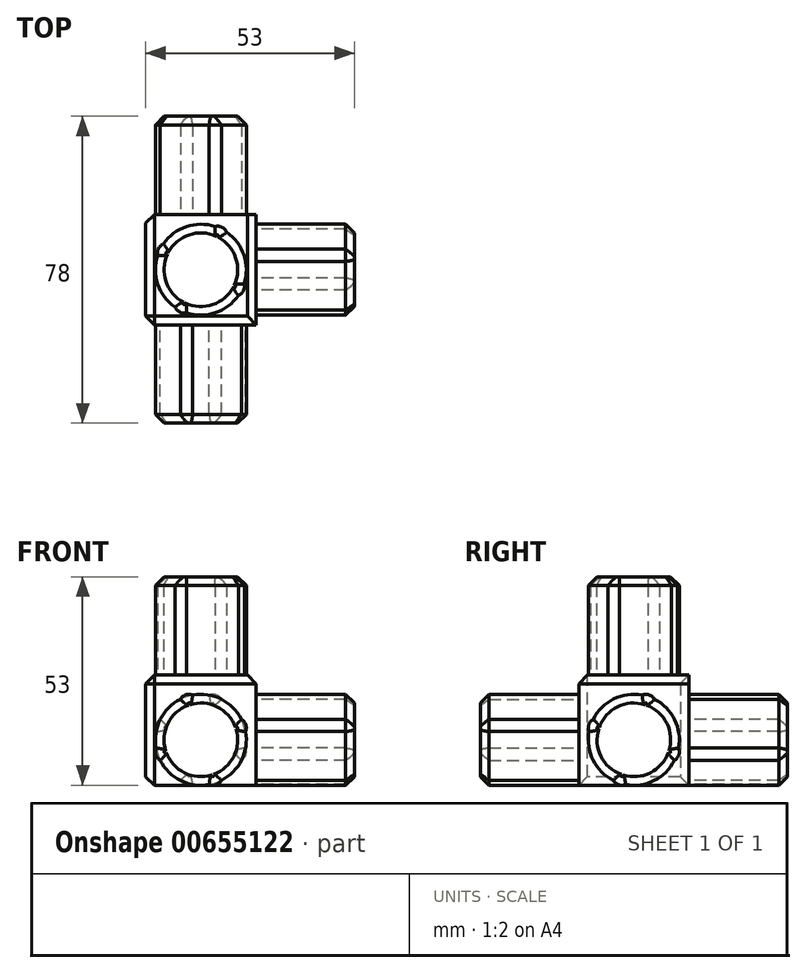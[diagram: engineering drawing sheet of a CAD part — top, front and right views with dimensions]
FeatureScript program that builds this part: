
annotation { "Feature Type Name" : "Feature", "Feature Type Description" : "" }
export const myFeature = defineFeature(function(context is Context, id is Id, definition is map)
    precondition{}
    {
        {
            var Q0;
            Q0=qCreatedBy(makeId("Front.planeOp"),FACE);
            var sketch = newSketch(context, id + "F0", { "sketchPlane" : qUnion([Q0])});
            skLineSegment(sketch, "E0.bottom", {"start": v(-14, 0) * mm, "end": v(14, 0) * mm});
            skLineSegment(sketch, "E0.top", {"start": v(-14, 28) * mm, "end": v(14, 28) * mm});
            skLineSegment(sketch, "E0.left", {"start": v(-14, 0) * mm, "end": v(-14, 28) * mm});
            skLineSegment(sketch, "E0.right", {"start": v(14, 0) * mm, "end": v(14, 28) * mm});
            skSolve(sketch);
        }
        {
            var Q0;
            Q0=qSketchRegion(id+"F0",true);
            extrude(context, id + "F1", {"entities" : qUnion([Q0]), "depth" : 28 * mm, "offsetDistance" : 25 * mm, "symmetric" : true});
        }
        {
            var Q0;
            Q0=makeQuery(id+"F1.opExtrude","CAP_FACE",FACE,{"disambiguationData":[OSD([sQuery(id+"F0.wireOp",EDGE,"E0.bottom"),sQuery(id+"F0.wireOp",EDGE,"E0.top"),sQuery(id+"F0.wireOp",EDGE,"E0.left"),sQuery(id+"F0.wireOp",EDGE,"E0.right")])],"isStart":false});
            var sketch = newSketch(context, id + "F2", { "sketchPlane" : qUnion([Q0])});
            skArc(sketch, "E1", {"start": v(-10.3, 6.34) * mm, "mid": v(-5.13, 1.2) * mm, "end": v(2.1, 0.2) * mm});
            skArc(sketch, "E2", {"start": v(-11.36, 9.46) * mm, "mid": v(-11.42, 7.7) * mm, "end": v(-10.3, 6.34) * mm});
            skArc(sketch, "E3.1.0", {"start": v(2.1, 0.2) * mm, "mid": v(3.85, 0.13) * mm, "end": v(5.2, 1.24) * mm});
            skArc(sketch, "E3.2.0", {"start": v(11.36, 13.64) * mm, "mid": v(11.42, 15.4) * mm, "end": v(10.3, 16.76) * mm});
            skArc(sketch, "E4.1.3.0", {"start": v(-2.1, 22.9) * mm, "mid": v(-3.85, 22.97) * mm, "end": v(-5.2, 21.86) * mm});
            skArc(sketch, "E5.trimOffspring", {"start": v(-5.2, 21.86) * mm, "mid": v(-10.35, 16.68) * mm, "end": v(-11.36, 9.46) * mm});
            skArc(sketch, "E6.trimOffspring", {"start": v(10.3, 16.76) * mm, "mid": v(5.13, 21.9) * mm, "end": v(-2.1, 22.9) * mm});
            skArc(sketch, "E7.trimOffspring", {"start": v(5.2, 1.24) * mm, "mid": v(10.35, 6.42) * mm, "end": v(11.36, 13.64) * mm});
            skSolve(sketch);
        }
        {
            var Q0;
            Q0=makeQuery(id+"F2.imprint","IMPRINT",FACE,{"disambiguationData":[TD([[makeQuery(id+"F2.imprint","IMPRINT",EDGE,{"derivedFrom":sQuery(id+"F2.wireOp",EDGE,"E1")}),1.0]])]});
            extrude(context, id + "F3", {"entities" : qUnion([Q0]), "operationType" : NewBodyOperationType.ADD, "depth" : 25 * mm, "offsetDistance" : 25 * mm});
        }
        {
            var Q0;
            Q0=makeQuery(id+"F1.opExtrude","SWEPT_FACE",FACE,{"disambiguationData":[OSD([sQuery(id+"F0.wireOp",EDGE,"E0.right")])]});
            var sketch = newSketch(context, id + "F4", { "sketchPlane" : qUnion([Q0])});
            skArc(sketch, "E8", {"start": v(-11.36, 13.64) * mm, "mid": v(-10.35, 6.42) * mm, "end": v(-5.2, 1.24) * mm});
            skArc(sketch, "E9", {"start": v(-10.3, 16.76) * mm, "mid": v(-11.42, 15.4) * mm, "end": v(-11.36, 13.64) * mm});
            skArc(sketch, "E10.1.0", {"start": v(-5.2, 1.24) * mm, "mid": v(-3.85, 0.13) * mm, "end": v(-2.1, 0.2) * mm});
            skArc(sketch, "E10.2.0", {"start": v(10.3, 6.34) * mm, "mid": v(11.42, 7.7) * mm, "end": v(11.36, 9.46) * mm});
            skArc(sketch, "E10.3.0", {"start": v(5.2, 21.86) * mm, "mid": v(3.85, 22.97) * mm, "end": v(2.1, 22.9) * mm});
            skArc(sketch, "E11.trimOffspring", {"start": v(2.1, 22.9) * mm, "mid": v(-5.13, 21.9) * mm, "end": v(-10.3, 16.76) * mm});
            skArc(sketch, "E12.trimOffspring", {"start": v(11.36, 9.46) * mm, "mid": v(10.35, 16.68) * mm, "end": v(5.2, 21.86) * mm});
            skArc(sketch, "E13.trimOffspring", {"start": v(-2.1, 0.2) * mm, "mid": v(5.13, 1.2) * mm, "end": v(10.3, 6.34) * mm});
            skSolve(sketch);
        }
        {
            var Q0;
            Q0=qSketchRegion(id+"F4",true);
            extrude(context, id + "F5", {"entities" : qUnion([Q0]), "operationType" : NewBodyOperationType.ADD, "depth" : 25 * mm, "offsetDistance" : 25 * mm});
        }
        {
            var Q0;
            Q0=makeQuery(id+"F1.opExtrude","SWEPT_FACE",FACE,{"disambiguationData":[OSD([sQuery(id+"F0.wireOp",EDGE,"E0.top")])]});
            var sketch = newSketch(context, id + "F6", { "sketchPlane" : qUnion([Q0])});
            skArc(sketch, "E14", {"start": v(-10.97, 3.6) * mm, "mid": v(-10.95, -3.69) * mm, "end": v(-6.55, -9.51) * mm});
            skArc(sketch, "E15", {"start": v(-9.51, 6.55) * mm, "mid": v(-10.8, 5.35) * mm, "end": v(-10.97, 3.6) * mm});
            skArc(sketch, "E16.1.0", {"start": v(-6.55, -9.51) * mm, "mid": v(-5.35, -10.8) * mm, "end": v(-3.6, -10.97) * mm});
            skArc(sketch, "E16.2.0", {"start": v(9.51, -6.55) * mm, "mid": v(10.8, -5.35) * mm, "end": v(10.97, -3.6) * mm});
            skArc(sketch, "E16.3.0", {"start": v(6.55, 9.51) * mm, "mid": v(5.35, 10.8) * mm, "end": v(3.6, 10.97) * mm});
            skArc(sketch, "E17.trimOffspring", {"start": v(-3.6, -10.97) * mm, "mid": v(3.69, -10.95) * mm, "end": v(9.51, -6.55) * mm});
            skArc(sketch, "E18.trimOffspring", {"start": v(10.97, -3.6) * mm, "mid": v(10.95, 3.69) * mm, "end": v(6.55, 9.51) * mm});
            skArc(sketch, "E19.trimOffspring", {"start": v(3.6, 10.97) * mm, "mid": v(-3.69, 10.95) * mm, "end": v(-9.51, 6.55) * mm});
            skSolve(sketch);
        }
        {
            var Q0;
            Q0=makeQuery(id+"F6.imprint","IMPRINT",FACE,{"disambiguationData":[TD([[makeQuery(id+"F6.imprint","IMPRINT",EDGE,{"derivedFrom":sQuery(id+"F6.wireOp",EDGE,"E14")}),1.0]])]});
            extrude(context, id + "F7", {"entities" : qUnion([Q0]), "operationType" : NewBodyOperationType.ADD, "depth" : 25 * mm, "offsetDistance" : 25 * mm});
        }
        {
            var Q0;
            Q0=makeQuery(id+"F1.opExtrude","CAP_FACE",FACE,{"disambiguationData":[OSD([sQuery(id+"F0.wireOp",EDGE,"E0.bottom"),sQuery(id+"F0.wireOp",EDGE,"E0.top"),sQuery(id+"F0.wireOp",EDGE,"E0.left"),sQuery(id+"F0.wireOp",EDGE,"E0.right")])],"isStart":true});
            var sketch = newSketch(context, id + "F8", { "sketchPlane" : qUnion([Q0])});
            skArc(sketch, "E20", {"start": v(-10.3, 6.34) * mm, "mid": v(-5.13, 1.2) * mm, "end": v(2.1, 0.2) * mm});
            skArc(sketch, "E21", {"start": v(-11.36, 9.46) * mm, "mid": v(-11.42, 7.7) * mm, "end": v(-10.3, 6.34) * mm});
            skArc(sketch, "E22.1.0", {"start": v(2.1, 0.2) * mm, "mid": v(3.85, 0.13) * mm, "end": v(5.2, 1.24) * mm});
            skArc(sketch, "E22.2.0", {"start": v(11.36, 13.64) * mm, "mid": v(11.42, 15.4) * mm, "end": v(10.3, 16.76) * mm});
            skArc(sketch, "E23.1.3.0", {"start": v(-2.1, 22.9) * mm, "mid": v(-3.85, 22.97) * mm, "end": v(-5.2, 21.86) * mm});
            skArc(sketch, "E24.trimOffspring", {"start": v(-5.2, 21.86) * mm, "mid": v(-10.35, 16.68) * mm, "end": v(-11.36, 9.46) * mm});
            skArc(sketch, "E25.trimOffspring", {"start": v(10.3, 16.76) * mm, "mid": v(5.13, 21.9) * mm, "end": v(-2.1, 22.9) * mm});
            skArc(sketch, "E26.trimOffspring", {"start": v(5.2, 1.24) * mm, "mid": v(10.35, 6.42) * mm, "end": v(11.36, 13.64) * mm});
            skSolve(sketch);
        }
        {
            var Q0;
            {var subQ5=sQuery(id+"F8.wireOp",EDGE,"E21");Q0=makeQuery(id+"F8.imprint","IMPRINT",FACE,{"disambiguationData":[TD([[makeQuery(id+"F8.imprint","IMPRINT",EDGE,{"derivedFrom":subQ5}),1.0]])]});}
            extrude(context, id + "F9", {"entities" : qUnion([Q0]), "operationType" : NewBodyOperationType.ADD, "depth" : 25 * mm, "offsetDistance" : 25 * mm});
        }
        {
            var Q0;
            Q0=makeQuery(id+"F5.opExtrude","CAP_EDGE",EDGE,{"disambiguationData":[OSD([sQuery(id+"F4.wireOp",EDGE,"E8")])],"isStart":false});
            var Q1;
            Q1=makeQuery(id+"F3.opExtrude","CAP_EDGE",EDGE,{"disambiguationData":[OSD([sQuery(id+"F2.wireOp",EDGE,"E1")])],"isStart":false});
            var Q2;
            Q2=makeQuery(id+"F7.opExtrude","CAP_EDGE",EDGE,{"disambiguationData":[OSD([sQuery(id+"F6.wireOp",EDGE,"E14")])],"isStart":false});
            var Q3;
            Q3=makeQuery(id+"F1.opExtrude","SWEPT_FACE",FACE,{"disambiguationData":[OSD([sQuery(id+"F0.wireOp",EDGE,"E0.left")])]});
            var Q4;
            Q4=makeQuery(id+"F1.opExtrude","SWEPT_EDGE",EDGE,{"disambiguationData":[OSD([sQuery(id+"F0.wireOp",EDGE,"E0.top"),sQuery(id+"F0.wireOp",EDGE,"E0.right")])]});
            var Q5;
            Q5=makeQuery(id+"F1.opExtrude","CAP_EDGE",EDGE,{"disambiguationData":[OSD([sQuery(id+"F0.wireOp",EDGE,"E0.top")])],"isStart":false});
            var Q6;
            Q6=makeQuery(id+"F3.opExtrude","CAP_EDGE",EDGE,{"disambiguationData":[OSD([sQuery(id+"F2.wireOp",EDGE,"E5.trimOffspring")])],"isStart":false});
            var Q7;
            Q7=makeQuery(id+"F3.opExtrude","CAP_EDGE",EDGE,{"disambiguationData":[OSD([sQuery(id+"F2.wireOp",EDGE,"E2")])],"isStart":false});
            var Q8;
            Q8=makeQuery(id+"F3.opExtrude","CAP_FACE",FACE,{"disambiguationData":[OSD([sQuery(id+"F2.wireOp",EDGE,"E1"),sQuery(id+"F2.wireOp",EDGE,"E2"),sQuery(id+"F2.wireOp",EDGE,"E3.1.0"),sQuery(id+"F2.wireOp",EDGE,"E3.2.0"),sQuery(id+"F2.wireOp",EDGE,"E4.1.3.0"),sQuery(id+"F2.wireOp",EDGE,"E5.trimOffspring"),sQuery(id+"F2.wireOp",EDGE,"E6.trimOffspring"),sQuery(id+"F2.wireOp",EDGE,"E7.trimOffspring")])],"isStart":false});
            var Q9;
            Q9=makeQuery(id+"F5.opExtrude","CAP_FACE",FACE,{"disambiguationData":[OSD([sQuery(id+"F4.wireOp",EDGE,"E8"),sQuery(id+"F4.wireOp",EDGE,"E9"),sQuery(id+"F4.wireOp",EDGE,"E10.1.0"),sQuery(id+"F4.wireOp",EDGE,"E10.2.0"),sQuery(id+"F4.wireOp",EDGE,"E10.3.0"),sQuery(id+"F4.wireOp",EDGE,"E11.trimOffspring"),sQuery(id+"F4.wireOp",EDGE,"E12.trimOffspring"),sQuery(id+"F4.wireOp",EDGE,"E13.trimOffspring")])],"isStart":false});
            var Q10;
            Q10=makeQuery(id+"F7.opExtrude","CAP_FACE",FACE,{"disambiguationData":[OSD([sQuery(id+"F6.wireOp",EDGE,"E14"),sQuery(id+"F6.wireOp",EDGE,"E15"),sQuery(id+"F6.wireOp",EDGE,"E16.1.0"),sQuery(id+"F6.wireOp",EDGE,"E16.2.0"),sQuery(id+"F6.wireOp",EDGE,"E16.3.0"),sQuery(id+"F6.wireOp",EDGE,"E17.trimOffspring"),sQuery(id+"F6.wireOp",EDGE,"E18.trimOffspring"),sQuery(id+"F6.wireOp",EDGE,"E19.trimOffspring")])],"isStart":false});
            var Q11;
            Q11=makeQuery(id+"F9.opExtrude","CAP_FACE",FACE,{"disambiguationData":[OSD([sQuery(id+"F8.wireOp",EDGE,"E20"),sQuery(id+"F8.wireOp",EDGE,"E21"),sQuery(id+"F8.wireOp",EDGE,"E22.1.0"),sQuery(id+"F8.wireOp",EDGE,"E22.2.0"),sQuery(id+"F8.wireOp",EDGE,"E23.1.3.0"),sQuery(id+"F8.wireOp",EDGE,"E24.trimOffspring"),sQuery(id+"F8.wireOp",EDGE,"E25.trimOffspring"),sQuery(id+"F8.wireOp",EDGE,"E26.trimOffspring")])],"isStart":false});
            chamfer(context, id + "F10", {"entities" : qUnion([Q0, Q1, Q2, Q3, Q4, Q5, Q6, Q7, Q8, Q9, Q10, Q11]), "width" : 2.2 * mm, "tangentPropagation" : true});
        }
    });
